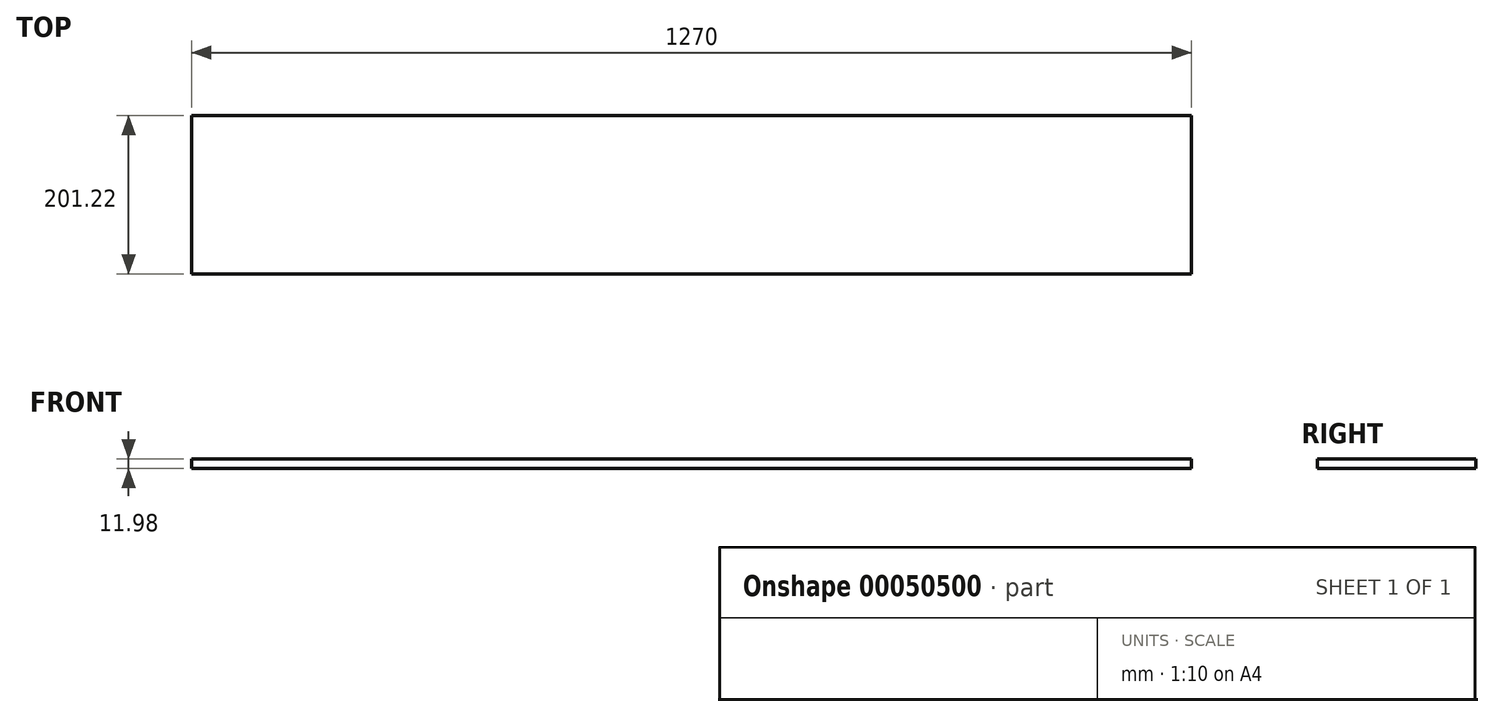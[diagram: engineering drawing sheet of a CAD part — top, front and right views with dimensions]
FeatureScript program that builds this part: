
annotation { "Feature Type Name" : "Feature", "Feature Type Description" : "" }
export const myFeature = defineFeature(function(context is Context, id is Id, definition is map)
    precondition{}
    {
        {
            var Q0;
            Q0=qCreatedBy(makeId("Top.planeOp"),FACE);
            var sketch = newSketch(context, id + "F0", { "sketchPlane" : qUnion([Q0])});
            skLineSegment(sketch, "E0.rect.bottom", {"start": v(635, 100.6) * mm, "end": v(-635, 100.6) * mm});
            skLineSegment(sketch, "E0.rect.top", {"start": v(635, -100.6) * mm, "end": v(-635, -100.6) * mm});
            skLineSegment(sketch, "E0.rect.left", {"start": v(635, 100.6) * mm, "end": v(635, -100.6) * mm});
            skLineSegment(sketch, "E0.rect.right", {"start": v(-635, 100.6) * mm, "end": v(-635, -100.6) * mm});
            skPoint(sketch, "E0.rect.middle", {"position": v(0, 0) * mm});
            skSolve(sketch);
        }
        {
            var Q0;
            Q0 = qSketchRegion(id + "F0", true);
            extrude(context, id + "F1", {"entities" : qUnion([Q0]), "endBound" : BoundingType.SYMMETRIC, "depth" : 12 * mm});
        }
    });
